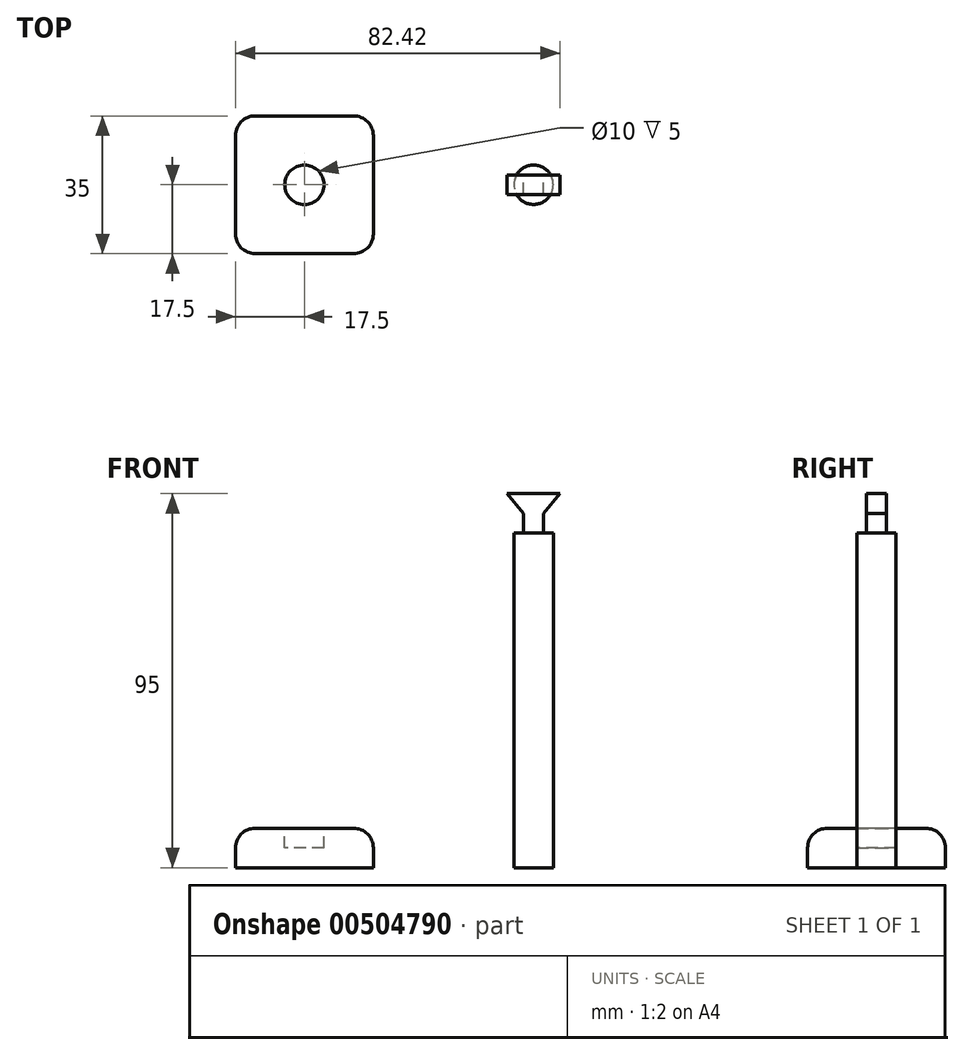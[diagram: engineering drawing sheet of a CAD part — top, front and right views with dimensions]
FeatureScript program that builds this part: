
annotation { "Feature Type Name" : "Feature", "Feature Type Description" : "" }
export const myFeature = defineFeature(function(context is Context, id is Id, definition is map)
    precondition{}
    {
        {
            var Q0;
            Q0=qCreatedBy(makeId("Top.planeOp"),FACE);
            var sketch = newSketch(context, id + "F0", { "sketchPlane" : qUnion([Q0])});
            skLineSegment(sketch, "E0.bottom", {"start": v(17.5, 17.5) * mm, "end": v(-17.5, 17.5) * mm});
            skLineSegment(sketch, "E0.top", {"start": v(17.5, -17.5) * mm, "end": v(-17.5, -17.5) * mm});
            skLineSegment(sketch, "E0.left", {"start": v(17.5, 17.5) * mm, "end": v(17.5, -17.5) * mm});
            skLineSegment(sketch, "E0.right", {"start": v(-17.5, 17.5) * mm, "end": v(-17.5, -17.5) * mm});
            skPoint(sketch, "E0.middle", {"position": v(0, 0) * mm});
            skSolve(sketch);
        }
        {
            var Q0;
            Q0=makeQuery(id+"F0.imprint","IMPRINT",FACE,{"disambiguationData":[TD([[makeQuery(id+"F0.imprint","IMPRINT",EDGE,{"derivedFrom":sQuery(id+"F0.wireOp",EDGE,"E0.bottom")}),1.0]])]});
            extrude(context, id + "F1", {"entities" : qUnion([Q0]), "depth" : 10 * mm});
        }
        {
            var Q0;
            Q0=makeQuery(id+"F1.opExtrude","CAP_EDGE",EDGE,{"disambiguationData":[OSD([sQuery(id+"F0.wireOp",EDGE,"E0.top")])],"isStart":false});
            var Q1;
            Q1=makeQuery(id+"F1.opExtrude","CAP_EDGE",EDGE,{"disambiguationData":[OSD([sQuery(id+"F0.wireOp",EDGE,"E0.right")])],"isStart":false});
            var Q2;
            Q2=makeQuery(id+"F1.opExtrude","CAP_EDGE",EDGE,{"disambiguationData":[OSD([sQuery(id+"F0.wireOp",EDGE,"E0.bottom")])],"isStart":false});
            var Q3;
            Q3=makeQuery(id+"F1.opExtrude","CAP_EDGE",EDGE,{"disambiguationData":[OSD([sQuery(id+"F0.wireOp",EDGE,"E0.left")])],"isStart":false});
            var Q4;
            Q4=makeQuery(id+"F1.opExtrude","SWEPT_EDGE",EDGE,{"disambiguationData":[OSD([sQuery(id+"F0.wireOp",EDGE,"E0.top"),sQuery(id+"F0.wireOp",EDGE,"E0.right")])]});
            var Q5;
            Q5=makeQuery(id+"F1.opExtrude","SWEPT_EDGE",EDGE,{"disambiguationData":[OSD([sQuery(id+"F0.wireOp",EDGE,"E0.top"),sQuery(id+"F0.wireOp",EDGE,"E0.left")])]});
            var Q6;
            Q6=makeQuery(id+"F1.opExtrude","SWEPT_EDGE",EDGE,{"disambiguationData":[OSD([sQuery(id+"F0.wireOp",EDGE,"E0.bottom"),sQuery(id+"F0.wireOp",EDGE,"E0.left")])]});
            var Q7;
            Q7=makeQuery(id+"F1.opExtrude","SWEPT_EDGE",EDGE,{"disambiguationData":[OSD([sQuery(id+"F0.wireOp",EDGE,"E0.bottom"),sQuery(id+"F0.wireOp",EDGE,"E0.right")])]});
            fillet(context, id + "F2", {"entities" : qUnion([Q0, Q1, Q2, Q3, Q4, Q5, Q6, Q7]), "radius" : 5 * mm, "tangentPropagation" : true, "allowEdgeOverflow" : false});
        }
        {
            var Q0;
            Q0=makeQuery(id+"F1.opExtrude","CAP_FACE",FACE,{"disambiguationData":[OSD([sQuery(id+"F0.wireOp",EDGE,"E0.bottom"),sQuery(id+"F0.wireOp",EDGE,"E0.top"),sQuery(id+"F0.wireOp",EDGE,"E0.left"),sQuery(id+"F0.wireOp",EDGE,"E0.right")])],"isStart":false});
            var sketch = newSketch(context, id + "F3", { "sketchPlane" : qUnion([Q0])});
            skCircle(sketch, "E1", {"center": v(0, 0) * mm, "radius": 5 * mm});
            skSolve(sketch);
        }
        {
            var Q0;
            Q0=makeQuery(id+"F3.imprint","IMPRINT",FACE,{"disambiguationData":[TD([[makeQuery(id+"F3.imprint","IMPRINT",EDGE,{"derivedFrom":sQuery(id+"F3.wireOp",EDGE,"E1")}),1.0]])]});
            extrude(context, id + "F4", {"entities" : qUnion([Q0]), "operationType" : NewBodyOperationType.REMOVE, "oppositeDirection" : true, "depth" : 5 * mm});
        }
        {
            var Q0;
            Q0=qCreatedBy(makeId("Top.planeOp"),FACE);
            var sketch = newSketch(context, id + "F5", { "sketchPlane" : qUnion([Q0])});
            skCircle(sketch, "E2", {"center": v(58.22, 0) * mm, "radius": 5 * mm});
            skSolve(sketch);
        }
        {
            var Q0;
            Q0=makeQuery(id+"F5.imprint","IMPRINT",FACE,{"disambiguationData":[TD([[makeQuery(id+"F5.imprint","IMPRINT",EDGE,{"derivedFrom":sQuery(id+"F5.wireOp",EDGE,"E2")}),1.0]])]});
            extrude(context, id + "F6", {"entities" : qUnion([Q0]), "depth" : 85 * mm});
        }
        {
            var Q0;
            Q0=qCreatedBy(makeId("Front.planeOp"),FACE);
            var sketch = newSketch(context, id + "F7", { "sketchPlane" : qUnion([Q0])});
            skLineSegment(sketch, "E3.bottom", {"start": v(60.72, 90) * mm, "end": v(55.72, 90) * mm});
            skLineSegment(sketch, "E3.top", {"start": v(60.72, 85) * mm, "end": v(55.72, 85) * mm});
            skLineSegment(sketch, "E3.left", {"start": v(60.72, 90) * mm, "end": v(60.72, 85) * mm});
            skLineSegment(sketch, "E3.right", {"start": v(55.72, 90) * mm, "end": v(55.72, 85) * mm});
            skPoint(sketch, "E3.middle", {"position": v(58.22, 87.5) * mm});
            skPoint(sketch, "E4", {"position": v(58.22, 85) * mm});
            skLineSegment(sketch, "E5.0", {"start": v(53.22, 85) * mm, "end": v(63.22, 85) * mm});
            skLineSegment(sketch, "E6", {"start": v(55.72, 90) * mm, "end": v(51.52, 95) * mm});
            skLineSegment(sketch, "E7", {"start": v(51.52, 95) * mm, "end": v(64.92, 95) * mm});
            skLineSegment(sketch, "E8", {"start": v(64.92, 95) * mm, "end": v(60.72, 90) * mm});
            skSolve(sketch);
        }
        {
            var Q0;
            Q0=makeQuery(id+"F7.imprint","IMPRINT",FACE,{"disambiguationData":[TD([[makeQuery(id+"F7.imprint","IMPRINT",EDGE,{"derivedFrom":sQuery(id+"F7.wireOp",EDGE,"E3.bottom")}),-1.0]])]});
            var Q1;
            Q1=makeQuery(id+"F7.imprint","IMPRINT",FACE,{"disambiguationData":[TD([[makeQuery(id+"F7.imprint","IMPRINT",EDGE,{"derivedFrom":sQuery(id+"F7.wireOp",EDGE,"E3.bottom")}),1.0]])]});
            extrude(context, id + "F8", {"entities" : qUnion([Q0, Q1]), "operationType" : NewBodyOperationType.ADD, "endBound" : BoundingType.SYMMETRIC, "depth" : 5 * mm});
        }
    });
